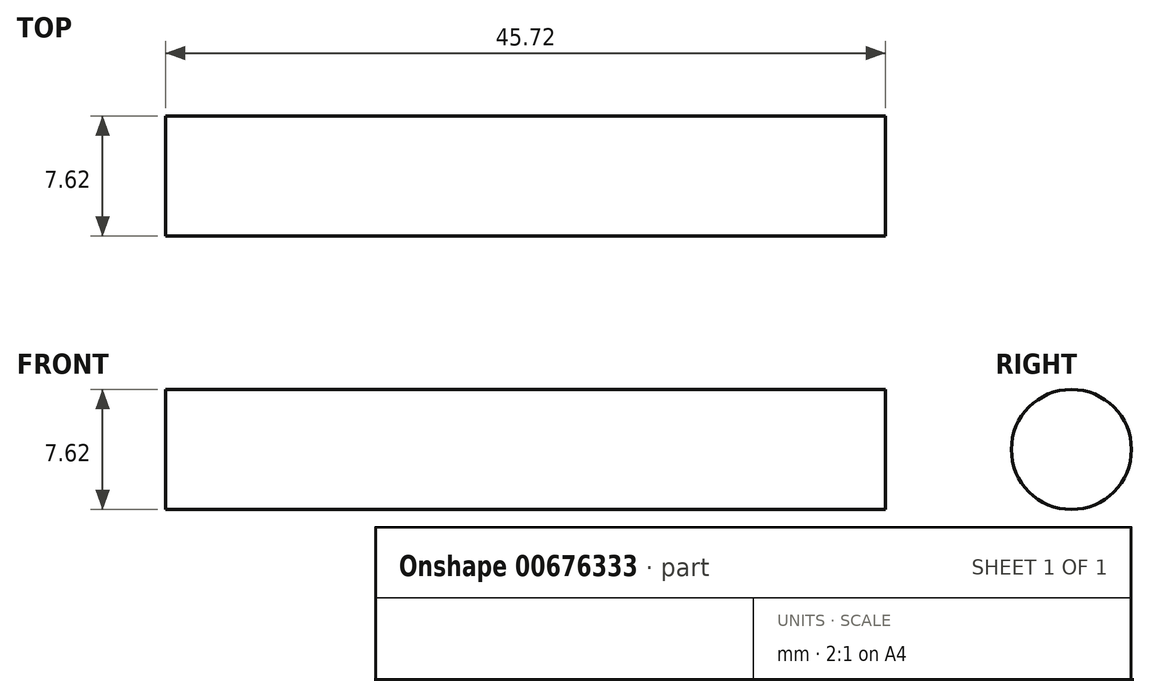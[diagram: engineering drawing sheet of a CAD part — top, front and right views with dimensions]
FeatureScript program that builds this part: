
annotation { "Feature Type Name" : "Feature", "Feature Type Description" : "" }
export const myFeature = defineFeature(function(context is Context, id is Id, definition is map)
    precondition{}
    {
        {
            var Q0;
            Q0=qCreatedBy(makeId("Right.planeOp"),FACE);
            var sketch = newSketch(context, id + "F0", { "sketchPlane" : qUnion([Q0])});
            skCircle(sketch, "E0", {"center": v(0, 0) * mm, "radius": 3.81 * mm});
            skSolve(sketch);
        }
        {
            var Q0;
            Q0 = qSketchRegion(id + "F0", true);
            extrude(context, id + "F1", {"entities" : qUnion([Q0]), "depth" : 45.72 * mm, "offsetDistance" : 25.4 * mm});
        }
    });
